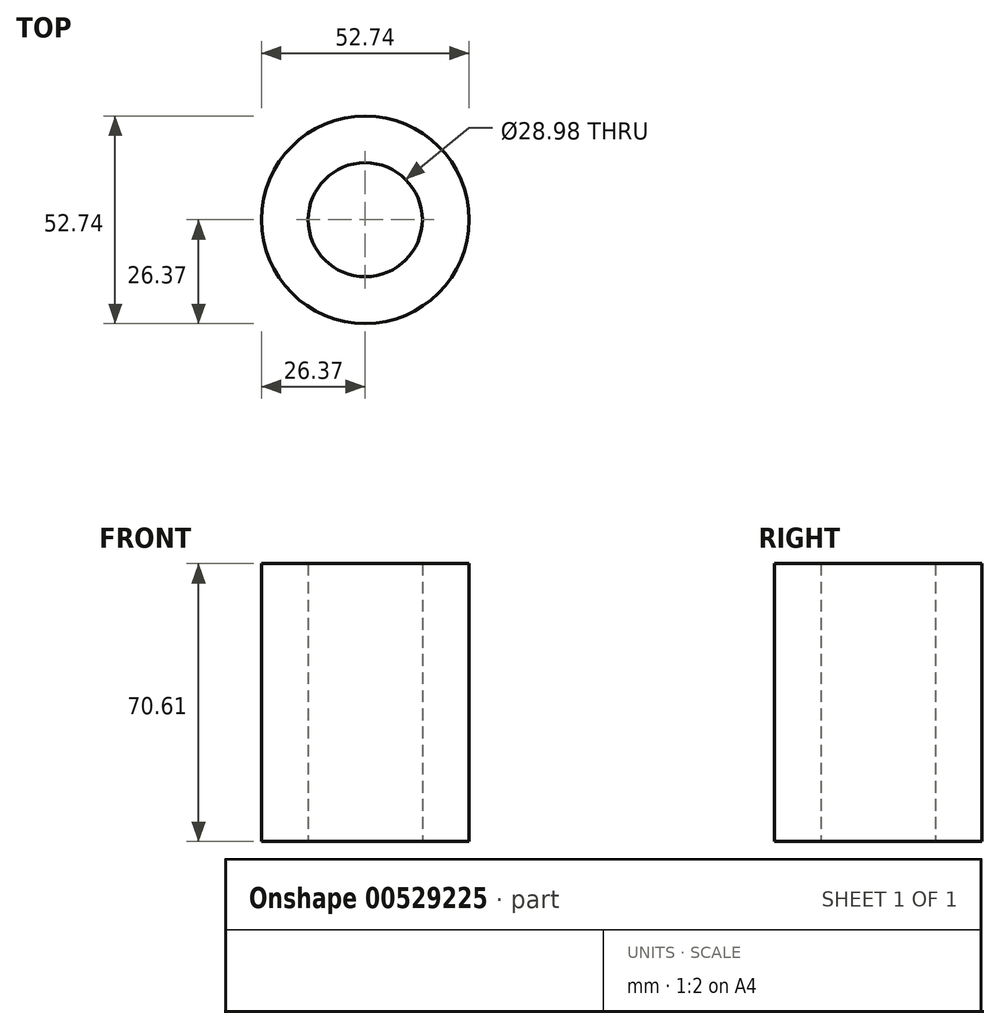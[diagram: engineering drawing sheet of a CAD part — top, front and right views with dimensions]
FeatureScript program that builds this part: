
annotation { "Feature Type Name" : "Feature", "Feature Type Description" : "" }
export const myFeature = defineFeature(function(context is Context, id is Id, definition is map)
    precondition{}
    {
        {
            var Q0;
            Q0=qCreatedBy(makeId("Top.planeOp"),FACE);
            var sketch = newSketch(context, id + "F0", { "sketchPlane" : qUnion([Q0])});
            skCircle(sketch, "E0", {"center": v(0, 0) * mm, "radius": 26.37 * mm});
            skCircle(sketch, "E1", {"center": v(0, 0) * mm, "radius": 14.5 * mm});
            skSolve(sketch);
        }
        {
            var Q0;
            Q0=makeQuery(id+"F0.imprint","IMPRINT",FACE,{"disambiguationData":[TD([[makeQuery(id+"F0.imprint","IMPRINT",EDGE,{"derivedFrom":sQuery(id+"F0.wireOp",EDGE,"E0")}),1.0]])]});
            extrude(context, id + "F1", {"entities" : qUnion([Q0]), "depth" : 70.61 * mm, "offsetDistance" : 25.4 * mm});
        }
    });
